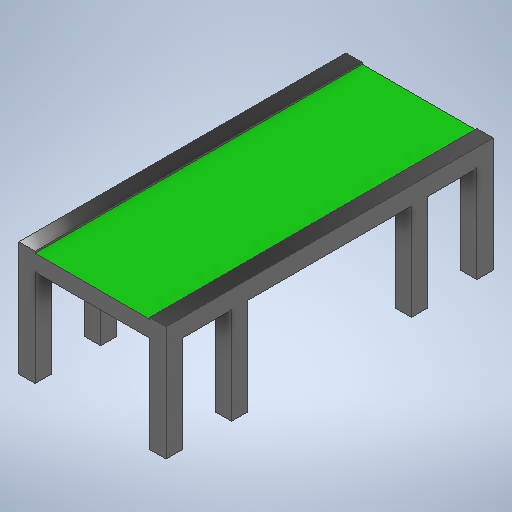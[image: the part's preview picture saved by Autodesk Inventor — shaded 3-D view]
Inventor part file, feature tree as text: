
AUTODESK INVENTOR PART (.ipt)
format: ipt  version: 2025.2 (Build 292293000, 293)  size: 334,336 bytes
history: native  units: mm
features: extrude x5, sketch x5
ambient origin geometry x8: Origin, YZ Plane, XZ Plane, XY Plane, X Axis, Y Axis, Z Axis, Center Point
bodies: Solid2 (feature_tree)
feature tree (10):
  extrude  "Extrusion6"  Depth=100.0mm
  extrude  "Extrusion7"  Depth=100.0mm TaperAngle=0.0deg
  extrude  "Extrusion9"  Depth=500.0mm
  extrude  "Extrusión11"  Depth=600.0mm
  extrude  "Extrusión12"  Depth=1500.0mm TaperAngle=0.0deg
  sketch  "Sketch9"  dims[d70=900.0mm d71=100.0mm]
  sketch  "Sketch10"  dims[d72=100.0mm d75=990.0mm d76=0.0mm]
  sketch  "Sketch13"  dims[d83=500.0mm d84=500.0mm]
  sketch  "Boceto15"  dims[d85=600.0mm d86=600.0mm]
  sketch  "Boceto16"  dims[d87=900.0mm d88=0.0mm d96=290.0mm d97=0.0mm d106=2000.0mm d108=1500.0mm d109=0.0mm d110=500.0mm d111=500.0mm d112=100.0mm d113=100.0mm d114=100.0mm d115=100.0mm d116=1500.0mm d117=0.0mm d53=0.5mm d54=0.872665mm d55=0.5mm d56=0.872665mm d102=0.5mm d103=0.872665mm d104=0.5mm d105=0.872665mm d118=0.5mm d119=0.872665mm d120=0.5mm d121=0.872665mm]
